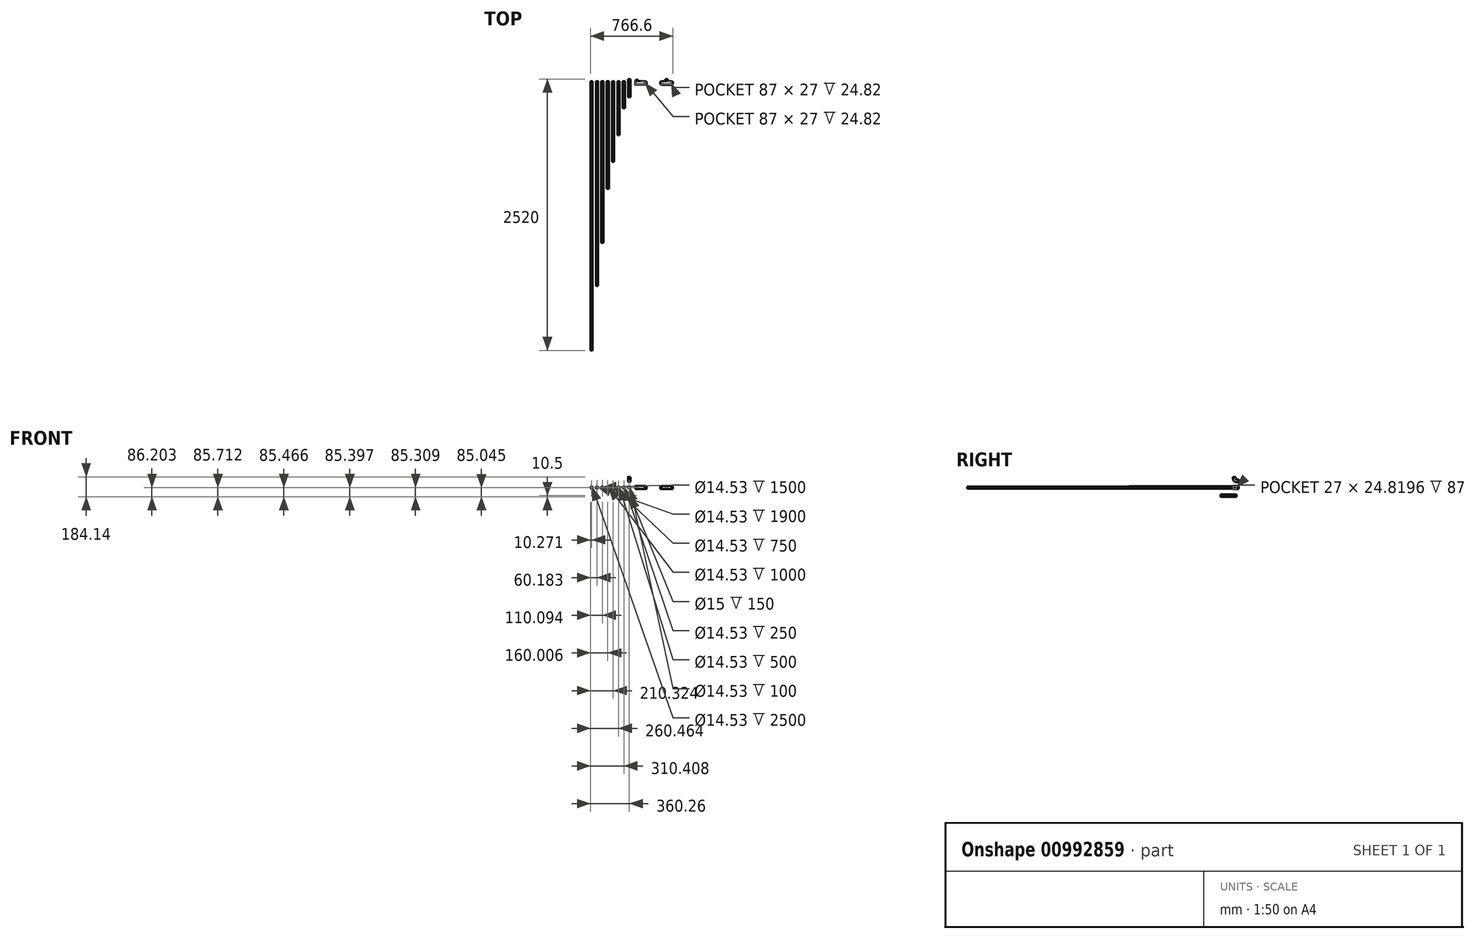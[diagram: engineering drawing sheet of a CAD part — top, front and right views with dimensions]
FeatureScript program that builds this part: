
annotation { "Feature Type Name" : "Feature", "Feature Type Description" : "" }
export const myFeature = defineFeature(function(context is Context, id is Id, definition is map)
    precondition{}
    {
        {
            var Q0;
            Q0=qCreatedBy(makeId("Front.planeOp"),FACE);
            var sketch = newSketch(context, id + "F0", { "sketchPlane" : qUnion([Q0])});
            skCircle(sketch, "E0", {"center": v(0, 0) * mm, "radius": 10.27 * mm});
            skCircle(sketch, "E1", {"center": v(0, 0) * mm, "radius": 7.26 * mm});
            skPoint(sketch, "E2", {"position": v(-350, 0) * mm});
            skPoint(sketch, "E3", {"position": v(-300, 0) * mm});
            skPoint(sketch, "E4", {"position": v(-250, 0) * mm});
            skPoint(sketch, "E5", {"position": v(-200, 0) * mm});
            skPoint(sketch, "E6", {"position": v(-150, 0) * mm});
            skPoint(sketch, "E7", {"position": v(-100, 0) * mm});
            skPoint(sketch, "E8", {"position": v(-50, 0) * mm});
            skCircle(sketch, "E9", {"center": v(-49.85, -0.1) * mm, "radius": 10.27 * mm});
            skCircle(sketch, "E10", {"center": v(-49.85, -0.1) * mm, "radius": 7.26 * mm});
            skCircle(sketch, "E11", {"center": v(-99.8, -0.2) * mm, "radius": 10.27 * mm});
            skCircle(sketch, "E12", {"center": v(-99.8, -0.2) * mm, "radius": 7.26 * mm});
            skCircle(sketch, "E13", {"center": v(-149.94, -0.46) * mm, "radius": 10.27 * mm});
            skCircle(sketch, "E14", {"center": v(-149.94, -0.46) * mm, "radius": 7.26 * mm});
            skCircle(sketch, "E15", {"center": v(-200.25, 0.7) * mm, "radius": 10.27 * mm});
            skCircle(sketch, "E16", {"center": v(-200.25, 0.7) * mm, "radius": 7.26 * mm});
            skCircle(sketch, "E17", {"center": v(-250.17, 0.21) * mm, "radius": 10.27 * mm});
            skCircle(sketch, "E18", {"center": v(-250.17, 0.21) * mm, "radius": 7.26 * mm});
            skCircle(sketch, "E19", {"center": v(-300.08, 0.21) * mm, "radius": 10.27 * mm});
            skCircle(sketch, "E20", {"center": v(-300.08, 0.21) * mm, "radius": 7.26 * mm});
            skCircle(sketch, "E21", {"center": v(-349.99, -0.03) * mm, "radius": 10.27 * mm});
            skCircle(sketch, "E22", {"center": v(-349.99, -0.03) * mm, "radius": 7.26 * mm});
            skPoint(sketch, "E23", {"position": v(100, 0) * mm});
            skLineSegment(sketch, "E24.bottom", {"start": v(145, 14) * mm, "end": v(55, 14) * mm});
            skLineSegment(sketch, "E24.top", {"start": v(145, -14) * mm, "end": v(55, -14) * mm});
            skLineSegment(sketch, "E24.left", {"start": v(145, 14) * mm, "end": v(145, -14) * mm});
            skLineSegment(sketch, "E24.right", {"start": v(55, 14) * mm, "end": v(55, -14) * mm});
            skCircle(sketch, "E25", {"center": v(69.74, 0) * mm, "radius": 10.5 * mm});
            skCircle(sketch, "E26", {"center": v(69.74, 0) * mm, "radius": 12.25 * mm});
            skLineSegment(sketch, "E27.bottom", {"start": v(143.5, 12.4) * mm, "end": v(56.5, 12.4) * mm});
            skLineSegment(sketch, "E27.top", {"start": v(143.5, -12.4) * mm, "end": v(56.5, -12.4) * mm});
            skLineSegment(sketch, "E27.left", {"start": v(143.5, 12.4) * mm, "end": v(143.5, -12.4) * mm});
            skLineSegment(sketch, "E27.right", {"start": v(56.5, 12.4) * mm, "end": v(56.5, -12.4) * mm});
            skCircle(sketch, "E28", {"center": v(0, 62.64) * mm, "radius": 12.5 * mm});
            skCircle(sketch, "E29", {"center": v(0, 62.64) * mm, "radius": 10.5 * mm});
            skPoint(sketch, "E30", {"position": v(0, -75) * mm});
            skCircle(sketch, "E31", {"center": v(0, -75) * mm, "radius": 10.5 * mm});
            skCircle(sketch, "E32", {"center": v(0, -75) * mm, "radius": 7.5 * mm});
            skPoint(sketch, "E33", {"position": v(346.34, 0) * mm});
            skLineSegment(sketch, "E34.bottom", {"start": v(391.34, 14) * mm, "end": v(301.34, 14) * mm});
            skLineSegment(sketch, "E34.top", {"start": v(391.34, -14) * mm, "end": v(301.34, -14) * mm});
            skLineSegment(sketch, "E34.left", {"start": v(391.34, 14) * mm, "end": v(391.34, -14) * mm});
            skLineSegment(sketch, "E34.right", {"start": v(301.34, 14) * mm, "end": v(301.34, -14) * mm});
            skCircle(sketch, "E35", {"center": v(346.34, 0) * mm, "radius": 10.5 * mm});
            skCircle(sketch, "E36", {"center": v(346.34, 0) * mm, "radius": 12.25 * mm});
            skLineSegment(sketch, "E37.bottom", {"start": v(389.84, 12.4) * mm, "end": v(302.84, 12.4) * mm});
            skLineSegment(sketch, "E37.top", {"start": v(389.84, -12.4) * mm, "end": v(302.84, -12.4) * mm});
            skLineSegment(sketch, "E37.left", {"start": v(389.84, 12.4) * mm, "end": v(389.84, -12.4) * mm});
            skLineSegment(sketch, "E37.right", {"start": v(302.84, 12.4) * mm, "end": v(302.84, -12.4) * mm});
            skSolve(sketch);
        }
        {
            var Q0;
            Q0=makeQuery(id+"F0.imprint","IMPRINT",FACE,{"disambiguationData":[TD([[makeQuery(id+"F0.imprint","IMPRINT",EDGE,{"derivedFrom":sQuery(id+"F0.wireOp",EDGE,"E0")}),1.0]])]});
            extrude(context, id + "F1", {"entities" : qUnion([Q0]), "depth" : 100 * mm, "offsetDistance" : 25 * mm});
        }
        {
            var Q0;
            Q0=makeQuery(id+"F0.imprint","IMPRINT",FACE,{"disambiguationData":[TD([[makeQuery(id+"F0.imprint","IMPRINT",EDGE,{"derivedFrom":sQuery(id+"F0.wireOp",EDGE,"E9")}),1.0]])]});
            extrude(context, id + "F2", {"entities" : qUnion([Q0]), "depth" : 250 * mm, "offsetDistance" : 25 * mm});
        }
        {
            var Q0;
            Q0=makeQuery(id+"F0.imprint","IMPRINT",FACE,{"disambiguationData":[TD([[makeQuery(id+"F0.imprint","IMPRINT",EDGE,{"derivedFrom":sQuery(id+"F0.wireOp",EDGE,"E11")}),1.0]])]});
            extrude(context, id + "F3", {"entities" : qUnion([Q0]), "depth" : 500 * mm, "offsetDistance" : 25 * mm});
        }
        {
            var Q0;
            Q0=makeQuery(id+"F0.imprint","IMPRINT",FACE,{"disambiguationData":[TD([[makeQuery(id+"F0.imprint","IMPRINT",EDGE,{"derivedFrom":sQuery(id+"F0.wireOp",EDGE,"E13")}),1.0]])]});
            extrude(context, id + "F4", {"entities" : qUnion([Q0]), "depth" : 750 * mm, "offsetDistance" : 25 * mm});
        }
        {
            var Q0;
            Q0=makeQuery(id+"F0.imprint","IMPRINT",FACE,{"disambiguationData":[TD([[makeQuery(id+"F0.imprint","IMPRINT",EDGE,{"derivedFrom":sQuery(id+"F0.wireOp",EDGE,"E15")}),1.0]])]});
            extrude(context, id + "F5", {"entities" : qUnion([Q0]), "depth" : 1000 * mm, "offsetDistance" : 25 * mm});
        }
        {
            var Q0;
            Q0=makeQuery(id+"F0.imprint","IMPRINT",FACE,{"disambiguationData":[TD([[makeQuery(id+"F0.imprint","IMPRINT",EDGE,{"derivedFrom":sQuery(id+"F0.wireOp",EDGE,"E17")}),1.0]])]});
            extrude(context, id + "F6", {"entities" : qUnion([Q0]), "depth" : 1500 * mm, "offsetDistance" : 25 * mm});
        }
        {
            var Q0;
            Q0=makeQuery(id+"F0.imprint","IMPRINT",FACE,{"disambiguationData":[TD([[makeQuery(id+"F0.imprint","IMPRINT",EDGE,{"derivedFrom":sQuery(id+"F0.wireOp",EDGE,"E19")}),1.0]])]});
            extrude(context, id + "F7", {"entities" : qUnion([Q0]), "depth" : 1900 * mm, "offsetDistance" : 25 * mm});
        }
        {
            var Q0;
            Q0=makeQuery(id+"F0.imprint","IMPRINT",FACE,{"disambiguationData":[TD([[makeQuery(id+"F0.imprint","IMPRINT",EDGE,{"derivedFrom":sQuery(id+"F0.wireOp",EDGE,"E21")}),1.0]])]});
            extrude(context, id + "F8", {"entities" : qUnion([Q0]), "depth" : 2500 * mm, "offsetDistance" : 25 * mm});
        }
        {
            var Q0;
            Q0=makeQuery(id+"F0.imprint","IMPRINT",FACE,{"disambiguationData":[TD([[makeQuery(id+"F0.imprint","IMPRINT",EDGE,{"derivedFrom":sQuery(id+"F0.wireOp",EDGE,"E25")}),-1.0]])]});
            extrude(context, id + "F9", {"entities" : qUnion([Q0]), "oppositeDirection" : true, "depth" : 15 * mm, "offsetDistance" : 25 * mm});
        }
        {
            var Q0;
            Q0=makeQuery(id+"F0.imprint","IMPRINT",FACE,{"disambiguationData":[TD([[makeQuery(id+"F0.imprint","IMPRINT",EDGE,{"derivedFrom":sQuery(id+"F0.wireOp",EDGE,"E24.bottom")}),1.0]])]});
            var Q1;
            Q1=makeQuery(id+"F9.opExtrude","CAP_FACE",FACE,{"disambiguationData":[OSD([sQuery(id+"F0.wireOp",EDGE,"E25"),sQuery(id+"F0.wireOp",EDGE,"E26")])],"isStart":true});
            extrude(context, id + "F10", {"entities" : qUnion([Q0, Q1]), "operationType" : NewBodyOperationType.ADD, "depth" : 3 * mm, "offsetDistance" : 25 * mm});
        }
        {
            var Q0;
            Q0=makeQuery(id+"F0.imprint","IMPRINT",FACE,{"disambiguationData":[TD([[makeQuery(id+"F0.imprint","IMPRINT",EDGE,{"derivedFrom":sQuery(id+"F0.wireOp",EDGE,"E24.bottom")}),1.0]])]});
            extrude(context, id + "F11", {"entities" : qUnion([Q0]), "operationType" : NewBodyOperationType.ADD, "depth" : 30 * mm, "offsetDistance" : 25 * mm});
        }
        {
            var Q0;
            {var subQ0=sQuery(id+"F0.wireOp",EDGE,"E27.left");Q0=makeQuery(id+"F0.imprint","IMPRINT",FACE,{"disambiguationData":[TD([[makeQuery(id+"F0.imprint","IMPRINT",EDGE,{"derivedFrom":subQ0}),-1.0]])]});}
            var Q1;
            {var subQ5=sQuery(id+"F0.wireOp",EDGE,"E27.right");Q1=makeQuery(id+"F0.imprint","IMPRINT",FACE,{"disambiguationData":[TD([[makeQuery(id+"F0.imprint","IMPRINT",EDGE,{"derivedFrom":subQ5}),1.0]])]});}
            var Q2;
            Q2=makeQuery(id+"F0.imprint","IMPRINT",FACE,{"disambiguationData":[TD([[makeQuery(id+"F0.imprint","IMPRINT",EDGE,{"derivedFrom":sQuery(id+"F0.wireOp",EDGE,"E25")}),-1.0]])]});
            extrude(context, id + "F12", {"entities" : qUnion([Q0, Q1, Q2]), "operationType" : NewBodyOperationType.ADD, "depth" : 3 * mm, "offsetDistance" : 25 * mm});
        }
        {
            var Q0;
            Q0=makeQuery(id+"F11.opExtrude","CAP_FACE",FACE,{"disambiguationData":[OSD([sQuery(id+"F0.wireOp",EDGE,"E24.bottom"),sQuery(id+"F0.wireOp",EDGE,"E24.top"),sQuery(id+"F0.wireOp",EDGE,"E24.left"),sQuery(id+"F0.wireOp",EDGE,"E24.right"),sQuery(id+"F0.wireOp",EDGE,"E27.bottom"),sQuery(id+"F0.wireOp",EDGE,"E27.top"),sQuery(id+"F0.wireOp",EDGE,"E27.left"),sQuery(id+"F0.wireOp",EDGE,"E27.right")])],"isStart":false});
            var sketch = newSketch(context, id + "F13", { "sketchPlane" : qUnion([Q0])});
            skLineSegment(sketch, "E38.bottom", {"start": v(54.5, 14.5) * mm, "end": v(145.5, 14.5) * mm});
            skLineSegment(sketch, "E38.top", {"start": v(54.5, -14.5) * mm, "end": v(145.5, -14.5) * mm});
            skLineSegment(sketch, "E38.left", {"start": v(54.5, 14.5) * mm, "end": v(54.5, -14.5) * mm});
            skLineSegment(sketch, "E38.right", {"start": v(145.5, 14.5) * mm, "end": v(145.5, -14.5) * mm});
            skPoint(sketch, "E38.middle", {"position": v(105.28, 0) * mm});
            skSolve(sketch);
        }
        {
            var Q0;
            Q0 = qSketchRegion(id + "F13", true);
            extrude(context, id + "F14", {"entities" : qUnion([Q0]), "operationType" : NewBodyOperationType.ADD, "depth" : 2 * mm, "offsetDistance" : 25 * mm});
        }
        {
            var Q0;
            {var subQ0=sQuery(id+"F0.wireOp",EDGE,"E24.left");Q0=makeQuery(id+"F11.boolean.opBoolean","MERGE",FACE,{"derivedFrom":[makeQuery(id+"F10.opExtrude","SWEPT_FACE",FACE,{"disambiguationData":[OSD([subQ0])]}),makeQuery(id+"F11.opExtrude","SWEPT_FACE",FACE,{"disambiguationData":[OSD([subQ0])]})]});}
            cPlane(context, id + "F15", {"entities" : qUnion([Q0]), "cplaneType" : CPlaneType.OFFSET, "offset" : 0 * mm, "width" : 150 * mm, "height" : 150 * mm});
        }
        {
            var Q0;
            Q0=qCreatedBy(id+"F15.planeOp",FACE);
            var sketch = newSketch(context, id + "F16", { "sketchPlane" : qUnion([Q0])});
            skCircle(sketch, "E39", {"center": v(-15.14, 0) * mm, "radius": 12.5 * mm});
            skCircle(sketch, "E40", {"center": v(-15.14, 0) * mm, "radius": 10.5 * mm});
            skSolve(sketch);
        }
        {
            var Q0;
            Q0=makeQuery(id+"F16.imprint","IMPRINT",FACE,{"disambiguationData":[TD([[makeQuery(id+"F16.imprint","IMPRINT",EDGE,{"derivedFrom":sQuery(id+"F16.wireOp",EDGE,"E39")}),1.0]])]});
            extrude(context, id + "F17", {"entities" : qUnion([Q0]), "operationType" : NewBodyOperationType.ADD, "depth" : 15 * mm, "offsetDistance" : 25 * mm});
        }
        {
            var Q0;
            Q0=makeQuery(id+"F14.opExtrude","CAP_FACE",FACE,{"disambiguationData":[OSD([sQuery(id+"F13.wireOp",EDGE,"E38.bottom"),sQuery(id+"F13.wireOp",EDGE,"E38.top"),sQuery(id+"F13.wireOp",EDGE,"E38.left"),sQuery(id+"F13.wireOp",EDGE,"E38.right")])],"isStart":false});
            fillet(context, id + "F18", {"entities" : qUnion([Q0]), "tangentPropagation" : true, "radius" : 1 * mm, "defaultsChanged" : false, "vertexSettings" : [], "allowEdgeOverflow" : false});
        }
        {
            var Q0;
            Q0=makeQuery(id+"F0.imprint","IMPRINT",FACE,{"disambiguationData":[TD([[makeQuery(id+"F0.imprint","IMPRINT",EDGE,{"derivedFrom":sQuery(id+"F0.wireOp",EDGE,"E28")}),1.0]])]});
            extrude(context, id + "F19", {"entities" : qUnion([Q0]), "oppositeDirection" : true, "depth" : 20 * mm, "offsetDistance" : 25 * mm});
        }
        {
            var Q0;
            Q0=qCreatedBy(makeId("Right.planeOp"),FACE);
            var sketch = newSketch(context, id + "F20", { "sketchPlane" : qUnion([Q0])});
            skPoint(sketch, "E41", {"position": v(0, 62.64) * mm});
            skLineSegment(sketch, "E42.top", {"start": v(0, 83.64) * mm, "end": v(-21, 83.64) * mm});
            skLineSegment(sketch, "E42.left", {"start": v(0, 62.64) * mm, "end": v(0, 83.64) * mm});
            skArc(sketch, "E43", {"start": v(-21, 83.64) * mm, "mid": v(-14.85, 68.8) * mm, "end": v(0, 62.64) * mm});
            skLineSegment(sketch, "E44", {"start": v(-21, 83.64) * mm, "end": v(-21, 98.64) * mm});
            skSolve(sketch);
        }
        {
            var Q0;
            Q0=makeQuery(id+"F0.imprint","IMPRINT",FACE,{"disambiguationData":[TD([[makeQuery(id+"F0.imprint","IMPRINT",EDGE,{"derivedFrom":sQuery(id+"F0.wireOp",EDGE,"E28")}),1.0]])]});
            var Q1;
            Q1=sQuery(id+"F20.wireOp",EDGE,"E43");
            var Q2;
            Q2=sQuery(id+"F20.wireOp",EDGE,"E44");
            sweep(context, id + "F21", {"operationType" : NewBodyOperationType.ADD, "profiles" : qUnion([Q0]), "path" : qUnion([Q1, Q2])});
        }
        {
            var Q0;
            Q0=makeQuery(id+"F0.imprint","IMPRINT",FACE,{"disambiguationData":[TD([[makeQuery(id+"F0.imprint","IMPRINT",EDGE,{"derivedFrom":sQuery(id+"F0.wireOp",EDGE,"E31")}),1.0]])]});
            extrude(context, id + "F22", {"entities" : qUnion([Q0]), "depth" : 150 * mm, "offsetDistance" : 25 * mm});
        }
        {
            var Q0;
            Q0=makeQuery(id+"F0.imprint","IMPRINT",FACE,{"disambiguationData":[TD([[makeQuery(id+"F0.imprint","IMPRINT",EDGE,{"derivedFrom":sQuery(id+"F0.wireOp",EDGE,"E35")}),-1.0]])]});
            extrude(context, id + "F23", {"entities" : qUnion([Q0]), "oppositeDirection" : true, "depth" : 20 * mm, "offsetDistance" : 25 * mm});
        }
        {
            var Q0;
            Q0=makeQuery(id+"F0.imprint","IMPRINT",FACE,{"disambiguationData":[TD([[makeQuery(id+"F0.imprint","IMPRINT",EDGE,{"derivedFrom":sQuery(id+"F0.wireOp",EDGE,"E34.bottom")}),1.0]])]});
            var Q1;
            Q1=makeQuery(id+"F0.imprint","IMPRINT",FACE,{"disambiguationData":[TD([[makeQuery(id+"F0.imprint","IMPRINT",EDGE,{"derivedFrom":sQuery(id+"F0.wireOp",EDGE,"E36")}),-1.0]])]});
            var Q2;
            Q2=makeQuery(id+"F0.imprint","IMPRINT",FACE,{"disambiguationData":[TD([[makeQuery(id+"F0.imprint","IMPRINT",EDGE,{"derivedFrom":sQuery(id+"F0.wireOp",EDGE,"E35")}),-1.0]])]});
            extrude(context, id + "F24", {"entities" : qUnion([Q0, Q1, Q2]), "operationType" : NewBodyOperationType.ADD, "depth" : 3 * mm, "offsetDistance" : 25 * mm});
        }
        {
            var Q0;
            Q0=makeQuery(id+"F0.imprint","IMPRINT",FACE,{"disambiguationData":[TD([[makeQuery(id+"F0.imprint","IMPRINT",EDGE,{"derivedFrom":sQuery(id+"F0.wireOp",EDGE,"E34.bottom")}),1.0]])]});
            extrude(context, id + "F25", {"entities" : qUnion([Q0]), "operationType" : NewBodyOperationType.ADD, "depth" : 30 * mm, "offsetDistance" : 25 * mm});
        }
        {
            var Q0;
            {var subQ0=sQuery(id+"F0.wireOp",EDGE,"E34.left");Q0=makeQuery(id+"F25.boolean.opBoolean","MERGE",FACE,{"derivedFrom":[makeQuery(id+"F24.opExtrude","SWEPT_FACE",FACE,{"disambiguationData":[OSD([subQ0])]}),makeQuery(id+"F25.opExtrude","SWEPT_FACE",FACE,{"disambiguationData":[OSD([subQ0])]})]});}
            var sketch = newSketch(context, id + "F26", { "sketchPlane" : qUnion([Q0])});
            skCircle(sketch, "E45", {"center": v(-15.14, 0) * mm, "radius": 10.44 * mm});
            skCircle(sketch, "E46", {"center": v(-15.14, 0) * mm, "radius": 12.52 * mm});
            skSolve(sketch);
        }
        {
            var Q0;
            Q0=makeQuery(id+"F26.imprint","IMPRINT",FACE,{"disambiguationData":[TD([[makeQuery(id+"F26.imprint","IMPRINT",EDGE,{"derivedFrom":sQuery(id+"F26.wireOp",EDGE,"E45")}),-1.0]])]});
            extrude(context, id + "F27", {"entities" : qUnion([Q0]), "operationType" : NewBodyOperationType.ADD, "depth" : 15 * mm, "offsetDistance" : 25 * mm});
        }
        {
            var Q0;
            Q0=sQuery(id+"F26.wireOp",VERTEX,"E45.center");
            var Q1;
            Q1=makeQuery(id+"F23.opExtrude","SWEPT_BODY",BODY,{"disambiguationData":[OSD([sQuery(id+"F0.wireOp",EDGE,"E35"),sQuery(id+"F0.wireOp",EDGE,"E36")])]});
            hole(context, id + "F28", {"style" : HoleStyle.SIMPLE, "endStyle" : HoleEndStyle.BLIND, "holeDiameter" : 20.5 * mm, "majorDiameter" : 5 * mm, "holeDepth" : 100 * mm, "isTappedThrough" : true, "tappedDepth" : 12 * mm, "tapClearance" : 3, "locations" : qUnion([Q0]), "scope" : qUnion([Q1])});
        }
        {
            var Q0;
            {var subQ0=sQuery(id+"F0.wireOp",EDGE,"E34.right");Q0=makeQuery(id+"F25.boolean.opBoolean","MERGE",FACE,{"derivedFrom":[makeQuery(id+"F24.opExtrude","SWEPT_FACE",FACE,{"disambiguationData":[OSD([subQ0])]}),makeQuery(id+"F25.opExtrude","SWEPT_FACE",FACE,{"disambiguationData":[OSD([subQ0])]})]});}
            var sketch = newSketch(context, id + "F29", { "sketchPlane" : qUnion([Q0])});
            skCircle(sketch, "E47", {"center": v(15.14, 0) * mm, "radius": 10.25 * mm});
            skPoint(sketch, "E47.first.point", {"position": v(25.39, 0) * mm});
            skPoint(sketch, "E47.second.point", {"position": v(4.89, 0) * mm});
            skPoint(sketch, "E47.third.point", {"position": v(4.9, -0.33) * mm});
            skCircle(sketch, "E48", {"center": v(15.14, 0) * mm, "radius": 12.5 * mm});
            skSolve(sketch);
        }
        {
            var Q0;
            Q0=makeQuery(id+"F29.imprint","IMPRINT",FACE,{"disambiguationData":[TD([[makeQuery(id+"F29.imprint","IMPRINT",EDGE,{"derivedFrom":sQuery(id+"F29.wireOp",EDGE,"E47")}),-1.0]])]});
            extrude(context, id + "F30", {"entities" : qUnion([Q0]), "operationType" : NewBodyOperationType.ADD, "depth" : 15 * mm, "offsetDistance" : 25 * mm});
        }
        {
            var Q0;
            Q0=makeQuery(id+"F25.opExtrude","CAP_FACE",FACE,{"disambiguationData":[OSD([sQuery(id+"F0.wireOp",EDGE,"E34.bottom"),sQuery(id+"F0.wireOp",EDGE,"E34.top"),sQuery(id+"F0.wireOp",EDGE,"E34.left"),sQuery(id+"F0.wireOp",EDGE,"E34.right"),sQuery(id+"F0.wireOp",EDGE,"E37.bottom"),sQuery(id+"F0.wireOp",EDGE,"E37.top"),sQuery(id+"F0.wireOp",EDGE,"E37.left"),sQuery(id+"F0.wireOp",EDGE,"E37.right")])],"isStart":false});
            var sketch = newSketch(context, id + "F31", { "sketchPlane" : qUnion([Q0])});
            skLineSegment(sketch, "E49.bottom", {"start": v(300.84, 14.5) * mm, "end": v(391.84, 14.5) * mm});
            skLineSegment(sketch, "E49.top", {"start": v(300.84, -14.5) * mm, "end": v(391.84, -14.5) * mm});
            skLineSegment(sketch, "E49.left", {"start": v(300.84, 14.5) * mm, "end": v(300.84, -14.5) * mm});
            skLineSegment(sketch, "E49.right", {"start": v(391.84, 14.5) * mm, "end": v(391.84, -14.5) * mm});
            skSolve(sketch);
        }
        {
            var Q0;
            Q0=makeQuery(id+"F31.imprint","IMPRINT",FACE,{"disambiguationData":[TD([[makeQuery(id+"F31.imprint","IMPRINT",EDGE,{"derivedFrom":sQuery(id+"F31.wireOp",EDGE,"E49.bottom")}),-1.0]])]});
            var Q1;
            Q1=makeQuery(id+"F31.imprint","IMPRINT",FACE,{"disambiguationData":[TD([[makeQuery(id+"F31.imprint","IMPRINT",EDGE,{"derivedFrom":makeQuery(id+"F25.opExtrude","CAP_EDGE",EDGE,{"disambiguationData":[OSD([sQuery(id+"F0.wireOp",EDGE,"E34.bottom")])],"isStart":false})}),1.0]])]});
            var Q2;
            Q2=makeQuery(id+"F31.imprint","IMPRINT",FACE,{"disambiguationData":[TD([[makeQuery(id+"F31.imprint","IMPRINT",EDGE,{"derivedFrom":makeQuery(id+"F25.opExtrude","CAP_EDGE",EDGE,{"disambiguationData":[OSD([sQuery(id+"F0.wireOp",EDGE,"E37.bottom")])],"isStart":false})}),1.0]])]});
            extrude(context, id + "F32", {"entities" : qUnion([Q0, Q1, Q2]), "operationType" : NewBodyOperationType.ADD, "depth" : 3 * mm, "offsetDistance" : 25 * mm});
        }
        {
            var Q0;
            Q0=makeQuery(id+"F32.opExtrude","CAP_FACE",FACE,{"disambiguationData":[OSD([sQuery(id+"F31.wireOp",EDGE,"E49.bottom"),sQuery(id+"F31.wireOp",EDGE,"E49.top"),sQuery(id+"F31.wireOp",EDGE,"E49.left"),sQuery(id+"F31.wireOp",EDGE,"E49.right")])],"isStart":false});
            fillet(context, id + "F33", {"entities" : qUnion([Q0]), "tangentPropagation" : true, "radius" : 1 * mm, "defaultsChanged" : true, "vertexSettings" : [], "allowEdgeOverflow" : false});
        }
    });
